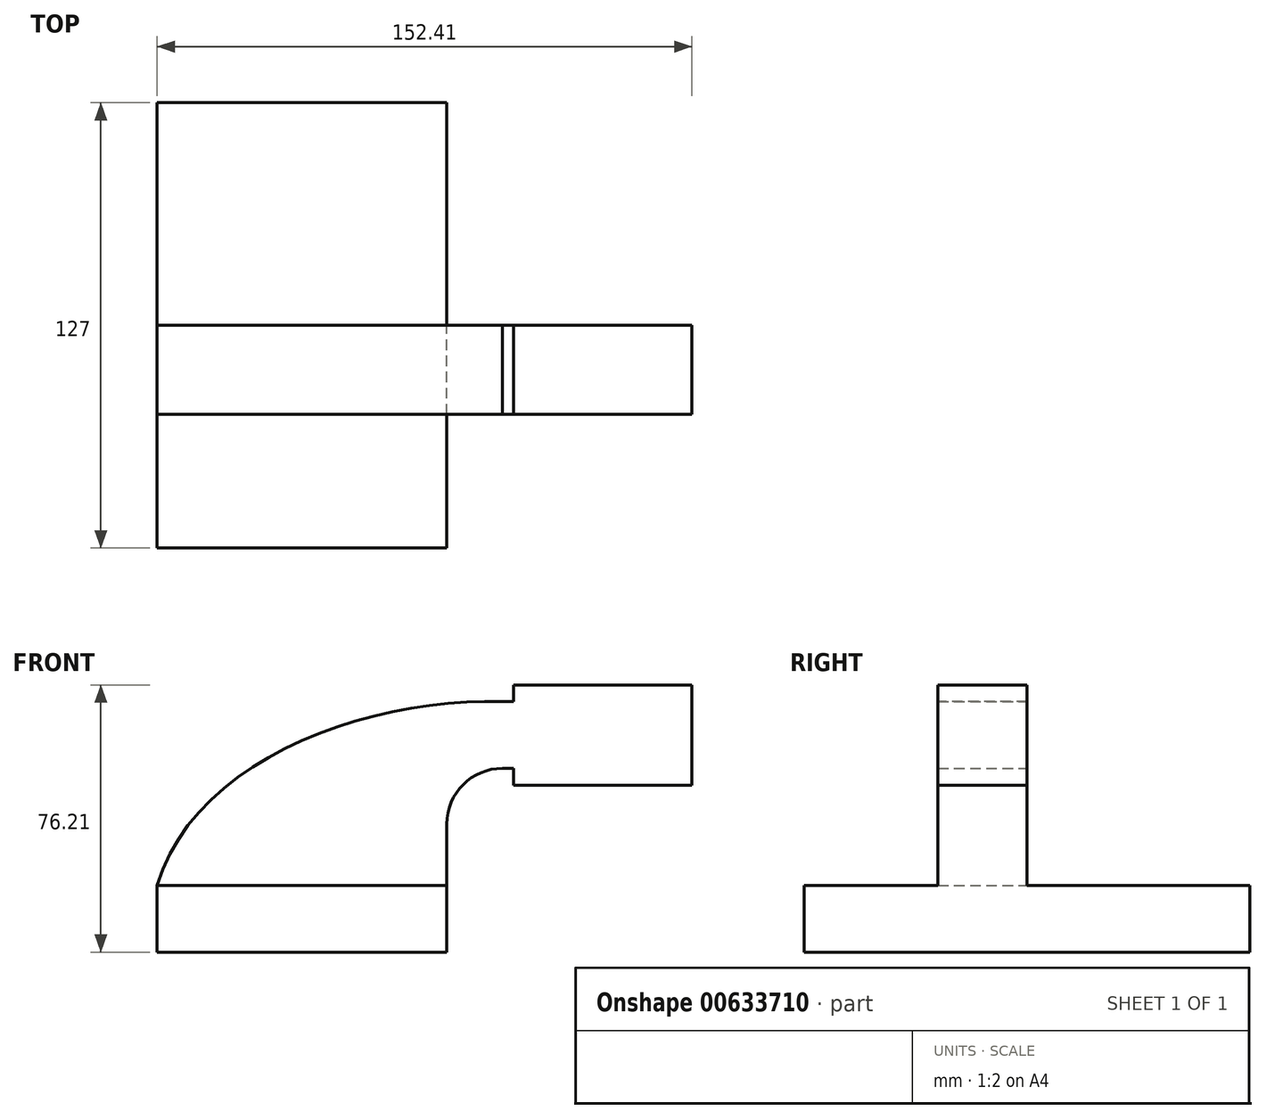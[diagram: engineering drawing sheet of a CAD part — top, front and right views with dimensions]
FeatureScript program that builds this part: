
annotation { "Feature Type Name" : "Feature", "Feature Type Description" : "" }
export const myFeature = defineFeature(function(context is Context, id is Id, definition is map)
    precondition{}
    {
        {
            var Q0;
            Q0=qCreatedBy(makeId("Front.planeOp"),FACE);
            var sketch = newSketch(context, id + "F0", { "sketchPlane" : qUnion([Q0])});
            skLineSegment(sketch, "E0.bottom", {"start": v(-41.28, 9.52) * mm, "end": v(41.28, 9.53) * mm});
            skLineSegment(sketch, "E0.top", {"start": v(-41.28, -9.52) * mm, "end": v(41.28, -9.52) * mm});
            skLineSegment(sketch, "E0.left", {"start": v(-41.28, 9.52) * mm, "end": v(-41.28, -9.53) * mm});
            skLineSegment(sketch, "E0.right", {"start": v(41.27, 9.53) * mm, "end": v(41.28, -9.52) * mm});
            skPoint(sketch, "E0.middle", {"position": v(0, 0) * mm});
            skLineSegment(sketch, "E1.bottom", {"start": v(60.32, 66.68) * mm, "end": v(111.12, 66.68) * mm});
            skLineSegment(sketch, "E1.top", {"start": v(60.32, 38.1) * mm, "end": v(111.12, 38.1) * mm});
            skLineSegment(sketch, "E1.left", {"start": v(60.32, 66.68) * mm, "end": v(60.32, 38.1) * mm});
            skLineSegment(sketch, "E1.right", {"start": v(111.12, 66.68) * mm, "end": v(111.12, 38.1) * mm});
            skPoint(sketch, "E1.middle", {"position": v(85.72, 52.39) * mm});
            skLineSegment(sketch, "E2", {"start": v(41.27, 9.53) * mm, "end": v(41.27, 27) * mm});
            skArc(sketch, "E3", {"start": v(41.27, 27) * mm, "mid": v(45.92, 38.23) * mm, "end": v(57.15, 42.88) * mm});
            skLineSegment(sketch, "E4", {"start": v(57.15, 42.88) * mm, "end": v(85.73, 42.88) * mm});
            skLineSegment(sketch, "E5.0", {"start": v(57.15, 61.93) * mm, "end": v(85.73, 61.93) * mm});
            skArc(sketch, "E5.1", {"start": v(22.22, 27) * mm, "mid": v(32.45, 51.7) * mm, "end": v(57.15, 61.93) * mm});
            skLineSegment(sketch, "E5.2", {"start": v(22.22, 9.53) * mm, "end": v(22.22, 27) * mm});
            skLineSegment(sketch, "E6", {"start": v(85.72, 38.1) * mm, "end": v(85.72, 66.68) * mm});
            skFitSpline(sketch, "E7", {"points": [v(-41.28, 9.52) * mm, v(57.15, 61.93) * mm], "startDerivative": vector(31.62, 107.3) * mm, "endDerivative": vector(115.42, -3.6) * mm});
            skSolve(sketch);
        }
        {
            var Q0;
            Q0=makeQuery(id+"F0.imprint","IMPRINT",FACE,{"disambiguationData":[TD([[makeQuery(id+"F0.imprint","IMPRINT",EDGE,{"derivedFrom":sQuery(id+"F0.wireOp",EDGE,"E0.top")}),1.0]])]});
            extrude(context, id + "F1", {"entities" : qUnion([Q0]), "endBound" : BoundingType.SYMMETRIC, "depth" : 127 * mm, "offsetDistance" : 25.4 * mm});
        }
        {
            var Q0;
            Q0 = qSketchRegion(id + "F0", true);
            extrude(context, id + "F2", {"entities" : qUnion([Q0]), "operationType" : NewBodyOperationType.ADD, "depth" : 25.4 * mm, "offsetDistance" : 25.4 * mm});
        }
    });
